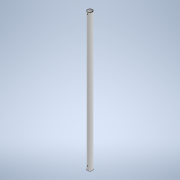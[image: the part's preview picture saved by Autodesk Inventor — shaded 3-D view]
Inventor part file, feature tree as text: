
AUTODESK INVENTOR PART (.ipt)
format: ipt  version: 2022 (Build 260153000, 153)  size: 174,080 bytes
history: native  units: mm
features: extrude x2, sketch x2
ambient origin geometry x8: Origin, YZ Plane, XZ Plane, XY Plane, X Axis, Y Axis, Z Axis, Center Point
bodies: Body1 (feature_tree)
feature tree (4):
  extrude  "Extrusion5"  Depth=18.0mm
  extrude  "Extrusion6"  Depth=10.0mm TaperAngle=0.0deg
  sketch  "Sketch2"  dims[d31=34.456mm d91=18.0mm]
  sketch  "Sketch3"  dims[d92=16.0mm d93=500.0mm d94=0.0mm d95=15.0mm d96=3.0mm d97=6.0mm d98=3.0mm d99=10.0mm d100=10.0mm d101=0.0mm d102=0.0mm]
